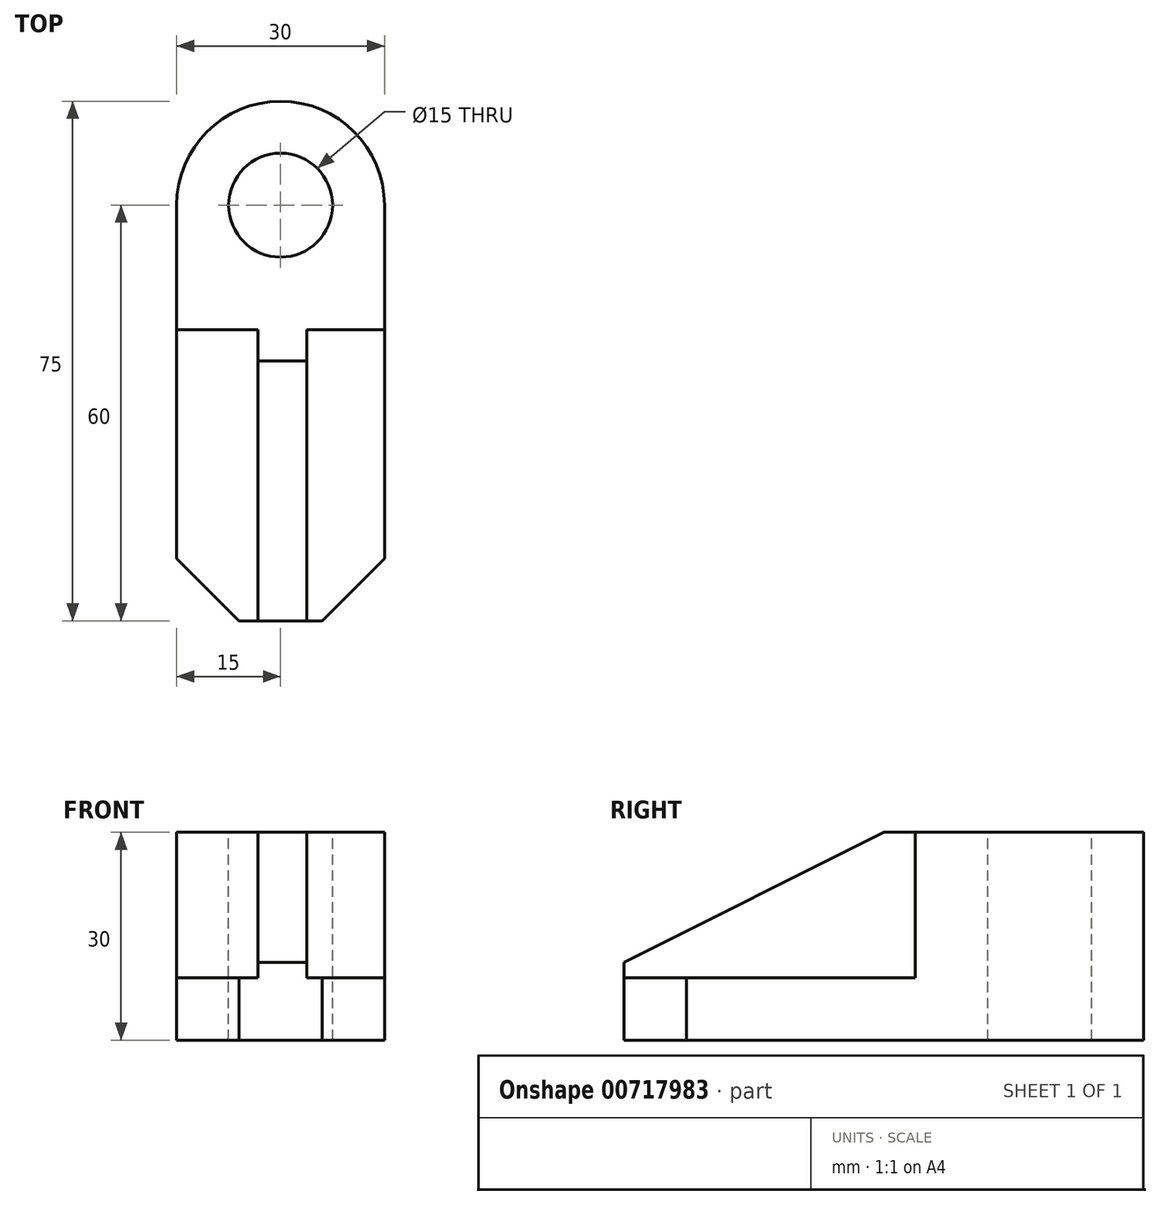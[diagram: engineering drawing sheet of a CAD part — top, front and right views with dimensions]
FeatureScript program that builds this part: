
annotation { "Feature Type Name" : "Feature", "Feature Type Description" : "" }
export const myFeature = defineFeature(function(context is Context, id is Id, definition is map)
    precondition{}
    {
        {
            var Q0;
            Q0=qCreatedBy(makeId("Top.planeOp"),FACE);
            var sketch = newSketch(context, id + "F0", { "sketchPlane" : qUnion([Q0])});
            skLineSegment(sketch, "E0.bottom", {"start": v(-15, 30) * mm, "end": v(15, 30) * mm});
            skLineSegment(sketch, "E0.top", {"start": v(-6, -30) * mm, "end": v(6, -30) * mm});
            skLineSegment(sketch, "E0.left", {"start": v(-15, 30) * mm, "end": v(-15, -21) * mm});
            skLineSegment(sketch, "E0.right", {"start": v(15, 30) * mm, "end": v(15, -21) * mm});
            skPoint(sketch, "E0.middle", {"position": v(0, 0) * mm});
            skLineSegment(sketch, "E1", {"start": v(-15, -21) * mm, "end": v(-6, -30) * mm});
            skPoint(sketch, "E2.orphan", {"position": v(-15, -30) * mm});
            skLineSegment(sketch, "E3", {"start": v(6, -30) * mm, "end": v(15, -21) * mm});
            skPoint(sketch, "E4.orphan", {"position": v(15, -30) * mm});
            skArc(sketch, "E5", {"start": v(15, 30) * mm, "mid": v(0, 45) * mm, "end": v(-15, 30) * mm});
            skSolve(sketch);
        }
        {
            var Q0;
            Q0=makeQuery(id+"F0.imprint","IMPRINT",FACE,{"disambiguationData":[TD([[makeQuery(id+"F0.imprint","IMPRINT",EDGE,{"derivedFrom":sQuery(id+"F0.wireOp",EDGE,"E0.bottom")}),-1.0]])]});
            extrude(context, id + "F1", {"entities" : qUnion([Q0]), "depth" : 9 * mm, "offsetDistance" : 25.4 * mm});
        }
        {
            var Q0;
            Q0=makeQuery(id+"F1.opExtrude","CAP_FACE",FACE,{"disambiguationData":[OSD([sQuery(id+"F0.wireOp",EDGE,"E0.bottom"),sQuery(id+"F0.wireOp",EDGE,"E0.top"),sQuery(id+"F0.wireOp",EDGE,"E0.left"),sQuery(id+"F0.wireOp",EDGE,"E0.right"),sQuery(id+"F0.wireOp",EDGE,"E1"),sQuery(id+"F0.wireOp",EDGE,"E3")])],"isStart":false});
            var sketch = newSketch(context, id + "F2", { "sketchPlane" : qUnion([Q0])});
            skLineSegment(sketch, "E6.bottom", {"start": v(-3.25, -30) * mm, "end": v(3.75, -30) * mm});
            skLineSegment(sketch, "E6.top", {"start": v(-3.25, 12) * mm, "end": v(3.75, 12) * mm});
            skLineSegment(sketch, "E6.left", {"start": v(-3.25, -30) * mm, "end": v(-3.25, 12) * mm});
            skLineSegment(sketch, "E6.right", {"start": v(3.75, -30) * mm, "end": v(3.75, 12) * mm});
            skSolve(sketch);
        }
        {
            var Q0;
            Q0=makeQuery(id+"F2.imprint","IMPRINT",FACE,{"disambiguationData":[TD([[makeQuery(id+"F2.imprint","IMPRINT",EDGE,{"derivedFrom":sQuery(id+"F2.wireOp",EDGE,"E6.bottom")}),1.0]])]});
            extrude(context, id + "F3", {"entities" : qUnion([Q0]), "operationType" : NewBodyOperationType.ADD, "depth" : 21 * mm, "offsetDistance" : 25 * mm});
        }
        {
            var Q0;
            Q0=makeQuery(id+"F3.opExtrude","SWEPT_FACE",FACE,{"disambiguationData":[OSD([sQuery(id+"F2.wireOp",EDGE,"E6.left")])]});
            var sketch = newSketch(context, id + "F4", { "sketchPlane" : qUnion([Q0])});
            skLineSegment(sketch, "E7", {"start": v(-10.92, 31.7) * mm, "end": v(31.08, 10.7) * mm});
            skSolve(sketch);
        }
        {
            var Q0;
            {var subQ0=sQuery(id+"F4.wireOp",EDGE,"E7");var subQ1=sQuery(id+"F2.wireOp",EDGE,"E6.left");var subQ4=makeQuery(id+"F3.opExtrude","CAP_EDGE",EDGE,{"disambiguationData":[OSD([subQ1])],"isStart":false});var subQ5=makeQuery(id+"F4.imprint","INTERSECT",VERTEX,{"derivedFrom":[subQ4,subQ0]});Q0=makeQuery(id+"F4.imprint","IMPRINT",FACE,{"disambiguationData":[TD([[makeQuery(id+"F4.imprint","IMPRINT",EDGE,{"disambiguationData":[TD([[subQ5,-1.0]])],"derivedFrom":subQ0}),1.0]])]});}
            extrude(context, id + "F5", {"entities" : qUnion([Q0]), "operationType" : NewBodyOperationType.REMOVE, "oppositeDirection" : true, "depth" : 25 * mm, "offsetDistance" : 25 * mm});
        }
        {
            var Q0;
            Q0=makeQuery(id+"F1.opExtrude","CAP_FACE",FACE,{"disambiguationData":[OSD([sQuery(id+"F0.wireOp",EDGE,"E0.bottom"),sQuery(id+"F0.wireOp",EDGE,"E0.top"),sQuery(id+"F0.wireOp",EDGE,"E0.left"),sQuery(id+"F0.wireOp",EDGE,"E0.right"),sQuery(id+"F0.wireOp",EDGE,"E1"),sQuery(id+"F0.wireOp",EDGE,"E3")])],"isStart":false});
            var sketch = newSketch(context, id + "F6", { "sketchPlane" : qUnion([Q0])});
            skLineSegment(sketch, "E8", {"start": v(15, 12) * mm, "end": v(-73.56, 12) * mm});
            skSolve(sketch);
        }
        {
            var Q0;
            Q0=makeQuery(id+"F0.imprint","IMPRINT",FACE,{"disambiguationData":[TD([[makeQuery(id+"F0.imprint","IMPRINT",EDGE,{"derivedFrom":sQuery(id+"F0.wireOp",EDGE,"E0.bottom")}),1.0]])]});
            extrude(context, id + "F7", {"entities" : qUnion([Q0]), "operationType" : NewBodyOperationType.ADD, "depth" : 30 * mm, "offsetDistance" : 25 * mm});
        }
        {
            var Q0;
            {var subQ0=makeQuery(id+"F1.opExtrude","CAP_EDGE",EDGE,{"disambiguationData":[OSD([sQuery(id+"F0.wireOp",EDGE,"E0.bottom")])],"isStart":false});Q0=makeQuery(id+"F6.imprint","IMPRINT",FACE,{"disambiguationData":[TD([[makeQuery(id+"F6.imprint","IMPRINT",EDGE,{"derivedFrom":subQ0}),-1.0]])]});}
            extrude(context, id + "F8", {"entities" : qUnion([Q0]), "operationType" : NewBodyOperationType.ADD, "depth" : 21 * mm, "offsetDistance" : 25 * mm});
        }
        {
            var Q0;
            {var subQ0=sQuery(id+"F0.wireOp",EDGE,"E0.bottom");Q0=makeQuery(id+"F8.boolean.opBoolean","MERGE",FACE,{"derivedFrom":[makeQuery(id+"F3.opExtrude","CAP_FACE",FACE,{"disambiguationData":[OSD([sQuery(id+"F2.wireOp",EDGE,"E6.bottom"),sQuery(id+"F2.wireOp",EDGE,"E6.top"),sQuery(id+"F2.wireOp",EDGE,"E6.left"),sQuery(id+"F2.wireOp",EDGE,"E6.right")])],"isStart":false}),makeQuery(id+"F7.opExtrude","CAP_FACE",FACE,{"disambiguationData":[OSD([subQ0,sQuery(id+"F0.wireOp",EDGE,"E5")])],"isStart":false}),makeQuery(id+"F8.opExtrude","CAP_FACE",FACE,{"disambiguationData":[OSD([subQ0,sQuery(id+"F0.wireOp",EDGE,"E0.left"),sQuery(id+"F0.wireOp",EDGE,"E0.right"),sQuery(id+"F6.wireOp",EDGE,"E8")])],"isStart":false})]});}
            var sketch = newSketch(context, id + "F9", { "sketchPlane" : qUnion([Q0])});
            skCircle(sketch, "E9", {"center": v(0, 30) * mm, "radius": 7.5 * mm});
            skSolve(sketch);
        }
        {
            var Q0;
            Q0=makeQuery(id+"F9.imprint","IMPRINT",FACE,{"disambiguationData":[TD([[makeQuery(id+"F9.imprint","IMPRINT",EDGE,{"derivedFrom":sQuery(id+"F9.wireOp",EDGE,"E9")}),1.0]])]});
            extrude(context, id + "F10", {"entities" : qUnion([Q0]), "operationType" : NewBodyOperationType.REMOVE, "oppositeDirection" : true, "depth" : 30 * mm, "offsetDistance" : 25 * mm});
        }
    });
